# Revit family: Б747 VoIP шлюз_RV17_LOD400 (05.11.23)
name_source: partatom
category: Электрооборудование
revit_build: Autodesk Revit 2017 (Build: 20170118_1100(x64)
units: mm (PartAtom-declared; Revit-internal decimal feet)

## family parameters
Всегда вертикально = Нет
Конфигурация панели = Два столбца, слева направо
На основе рабочей плоскости = Да
Общий = Нет
При загрузке вырезать с полостями = Нет
Размер круглого соединителя = Использовать диаметр
Тип детали = Щит
Точка расчета площади = Нет

## types (1)
- Б747 VoIP шлюз
    ADSK_URL страницы изделия = https://stilsoft.ru
    ADSK_Единица измерения = шт.
    ADSK_Завод-изготовитель = ООО «Основа Безопасности»
    ADSK_Количество = 1
    ADSK_Марка = СТВФ.426471.041
    ADSK_Масса = 0.5
    ADSK_Наименование = VoIP шлюз Б747
    ADSK_Размер_Высота = 44 мм
    ADSK_Размер_Глубина = 93 мм
    ADSK_Размер_Длина = 159 мм
    d_короба = 20 мм
    Диапазон напряжения электропитания постоянного тока, В = 12-24 (Passive РоЕ)
    Интерфейс связи = 10BaseT/100BaseTX Ethernet
    Напряжение = 12
    Отметка по умолчанию = 1219 мм
    Потребляемый ток при 12В / 24В, А = 0,6 / 0,2
    Режим работы = непрерывный
